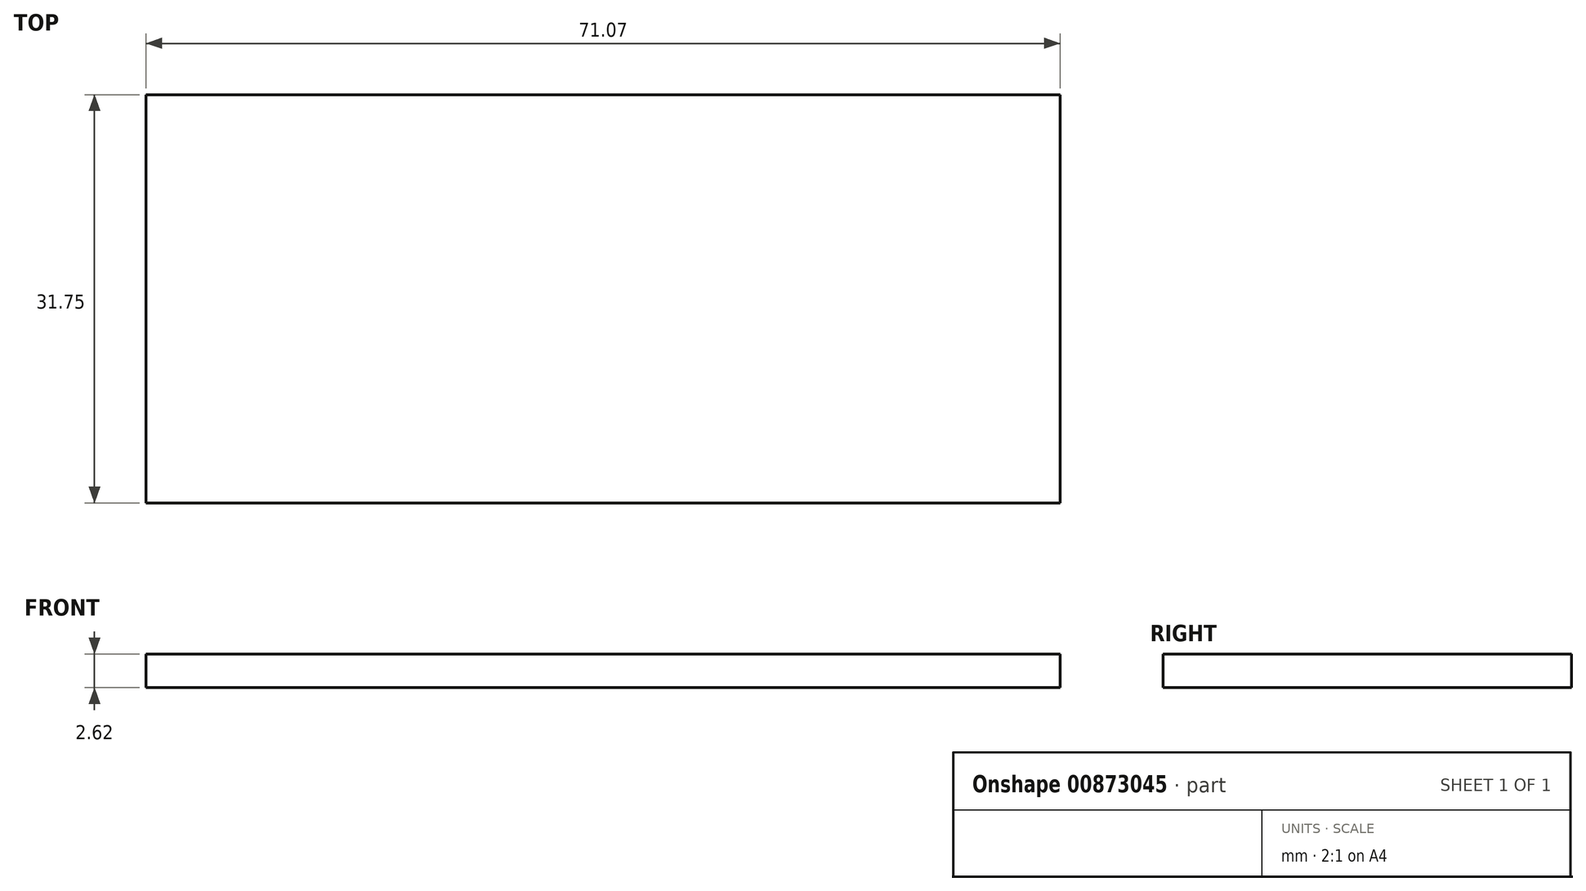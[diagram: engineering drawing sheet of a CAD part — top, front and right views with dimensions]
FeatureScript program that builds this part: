
annotation { "Feature Type Name" : "Feature", "Feature Type Description" : "" }
export const myFeature = defineFeature(function(context is Context, id is Id, definition is map)
    precondition{}
    {
        {
            var Q0;
            Q0=qCreatedBy(makeId("Front.planeOp"),FACE);
            var sketch = newSketch(context, id + "F0", { "sketchPlane" : qUnion([Q0])});
            skLineSegment(sketch, "E0.bottom", {"start": v(37.81, 44.23) * mm, "end": v(-33.26, 44.23) * mm});
            skLineSegment(sketch, "E0.top", {"start": v(37.81, 41.6) * mm, "end": v(-33.26, 41.6) * mm});
            skLineSegment(sketch, "E0.left", {"start": v(37.81, 44.23) * mm, "end": v(37.81, 41.6) * mm});
            skLineSegment(sketch, "E0.right", {"start": v(-33.26, 44.23) * mm, "end": v(-33.26, 41.6) * mm});
            skSolve(sketch);
        }
        {
            var Q0;
            Q0 = qSketchRegion(id + "F0", true);
            extrude(context, id + "F1", {"entities" : qUnion([Q0]), "depth" : 31.75 * mm, "offsetDistance" : 25.4 * mm});
        }
    });
